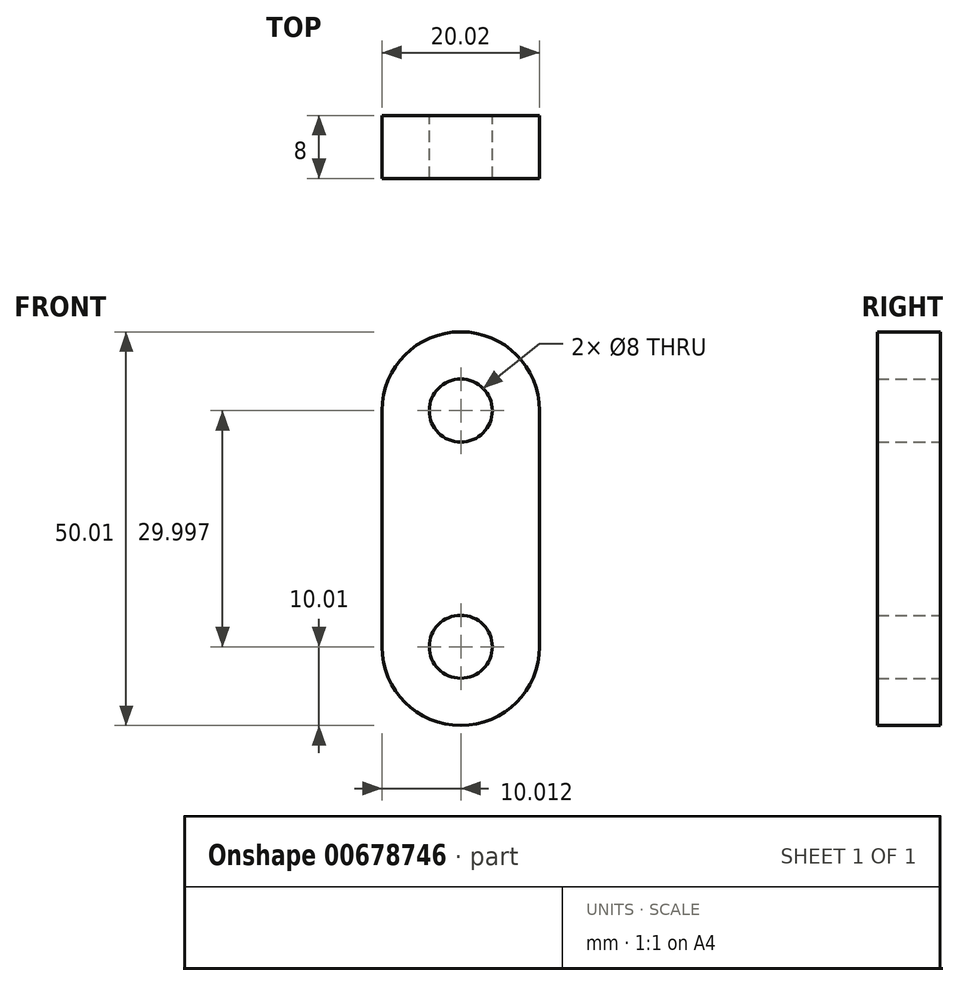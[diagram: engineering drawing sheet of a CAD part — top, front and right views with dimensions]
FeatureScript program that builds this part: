
annotation { "Feature Type Name" : "Feature", "Feature Type Description" : "" }
export const myFeature = defineFeature(function(context is Context, id is Id, definition is map)
    precondition{}
    {
        {
            var Q0;
            Q0=qCreatedBy(makeId("Front.planeOp"),FACE);
            var sketch = newSketch(context, id + "F0", { "sketchPlane" : qUnion([Q0])});
            skLineSegment(sketch, "E0.bottom", {"start": v(0, 0) * mm, "end": v(-20.02, 0) * mm});
            skLineSegment(sketch, "E0.top", {"start": v(0, 30) * mm, "end": v(-20.02, 30) * mm});
            skLineSegment(sketch, "E0.left", {"start": v(0, 0) * mm, "end": v(0, 30) * mm});
            skLineSegment(sketch, "E0.right", {"start": v(-20.02, 0) * mm, "end": v(-20.02, 30) * mm});
            skCircle(sketch, "E1", {"center": v(-10, 30) * mm, "radius": 10 * mm});
            skCircle(sketch, "E2", {"center": v(-10, 0) * mm, "radius": 10 * mm});
            skCircle(sketch, "E3", {"center": v(-10, 30) * mm, "radius": 4 * mm});
            skCircle(sketch, "E4", {"center": v(-10, 0) * mm, "radius": 4 * mm});
            skSolve(sketch);
        }
        {
            var Q0;
            {var subQ1=sQuery(id+"F0.wireOp",EDGE,"E0.top");var subQ3=sQuery(id+"F0.wireOp",EDGE,"E3");var subQ4=makeQuery(id+"F0.imprint","INTERSECT",VERTEX,{"disambiguationData":[OD(0.0)],"derivedFrom":[subQ1,subQ3]});Q0=makeQuery(id+"F0.imprint","IMPRINT",FACE,{"disambiguationData":[TD([[makeQuery(id+"F0.imprint","IMPRINT",EDGE,{"disambiguationData":[TD([[subQ4,-1.0]])],"derivedFrom":subQ3}),-1.0]])]});}
            var Q1;
            {var subQ1=sQuery(id+"F0.wireOp",EDGE,"E0.top");var subQ3=sQuery(id+"F0.wireOp",EDGE,"E3");var subQ4=makeQuery(id+"F0.imprint","INTERSECT",VERTEX,{"disambiguationData":[OD(0.0)],"derivedFrom":[subQ1,subQ3]});Q1=makeQuery(id+"F0.imprint","IMPRINT",FACE,{"disambiguationData":[TD([[makeQuery(id+"F0.imprint","IMPRINT",EDGE,{"disambiguationData":[TD([[subQ4,1.0]])],"derivedFrom":subQ3}),-1.0]])]});}
            var Q2;
            {var subQ0=sQuery(id+"F0.wireOp",EDGE,"E0.left");Q2=makeQuery(id+"F0.imprint","IMPRINT",FACE,{"disambiguationData":[TD([[makeQuery(id+"F0.imprint","IMPRINT",EDGE,{"derivedFrom":subQ0}),1.0]])]});}
            var Q3;
            {var subQ1=sQuery(id+"F0.wireOp",EDGE,"E0.bottom");var subQ3=sQuery(id+"F0.wireOp",EDGE,"E4");var subQ4=makeQuery(id+"F0.imprint","INTERSECT",VERTEX,{"disambiguationData":[OD(0.0)],"derivedFrom":[subQ1,subQ3]});Q3=makeQuery(id+"F0.imprint","IMPRINT",FACE,{"disambiguationData":[TD([[makeQuery(id+"F0.imprint","IMPRINT",EDGE,{"disambiguationData":[TD([[subQ4,-1.0]])],"derivedFrom":subQ3}),-1.0]])]});}
            var Q4;
            {var subQ1=sQuery(id+"F0.wireOp",EDGE,"E0.bottom");var subQ3=sQuery(id+"F0.wireOp",EDGE,"E4");var subQ4=makeQuery(id+"F0.imprint","INTERSECT",VERTEX,{"disambiguationData":[OD(0.0)],"derivedFrom":[subQ1,subQ3]});Q4=makeQuery(id+"F0.imprint","IMPRINT",FACE,{"disambiguationData":[TD([[makeQuery(id+"F0.imprint","IMPRINT",EDGE,{"disambiguationData":[TD([[subQ4,1.0]])],"derivedFrom":subQ3}),-1.0]])]});}
            extrude(context, id + "F1", {"entities" : qUnion([Q0, Q1, Q2, Q3, Q4]), "depth" : 8 * mm, "offsetDistance" : 25 * mm});
        }
    });
